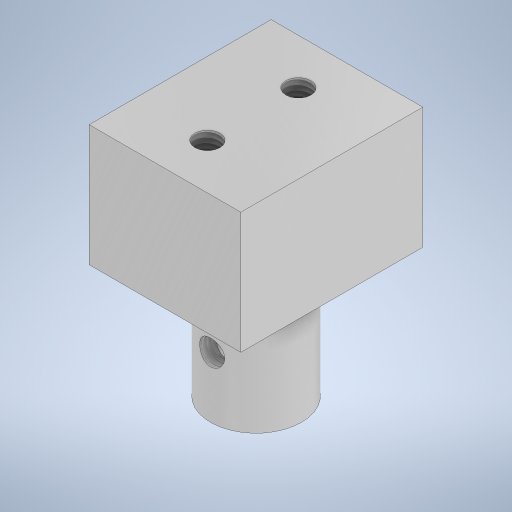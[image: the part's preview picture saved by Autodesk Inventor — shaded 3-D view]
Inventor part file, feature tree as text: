
AUTODESK INVENTOR PART (.ipt)
format: ipt  version: 2023.2 (Build 272271030, 271C)  size: 275,456 bytes
history: native  units: mm
features: sketch x4, extrude x2, hole x2, other x1
ambient origin geometry x8: Origin, YZ Plane, XZ Plane, XY Plane, X Axis, Y Axis, Z Axis, Center Point
bodies: Body1 (feature_tree)
feature tree (9):
  other  "Sólido1"
  extrude  "Extrusão1"  Depth=30.0mm
  hole  "Furo1"  [1 undecoded]
  extrude  "Extrusão2"  Depth=12.0mm
  hole  "Furo2"  [1 undecoded]
  sketch  "Esboço1"  dims[d0=25.0mm d1=30.0mm]
  sketch  "Esboço2"  dims[d2=20.0mm d3=0.0mm d4=25.0mm]
  sketch  "Esboço3"  dims[d5=12.0mm d6=12.0mm]
  sketch  "Esboço4"  dims[d9=4.134mm d10=10.0mm d11=4.0mm d12=2.0mm d13=90.0deg d14=14.2mm d15=20.594885mm d16=25.0mm d17=30.0mm d18=12.5mm d19=15.0mm d20=10.0mm d21=15.0mm d22=20.0mm d23=0.0mm d24=4.134mm d25=13.0mm d26=4.0mm d27=2.0mm d28=90.0deg d29=13.0mm d30=20.594885mm d31=7.5mm d32=7.5mm]
note: 2 required parameter values undecoded (feature->parameter linkage not recoverable at this tier; creation-order binding heuristic only, values carry confidence <= 0.55)
